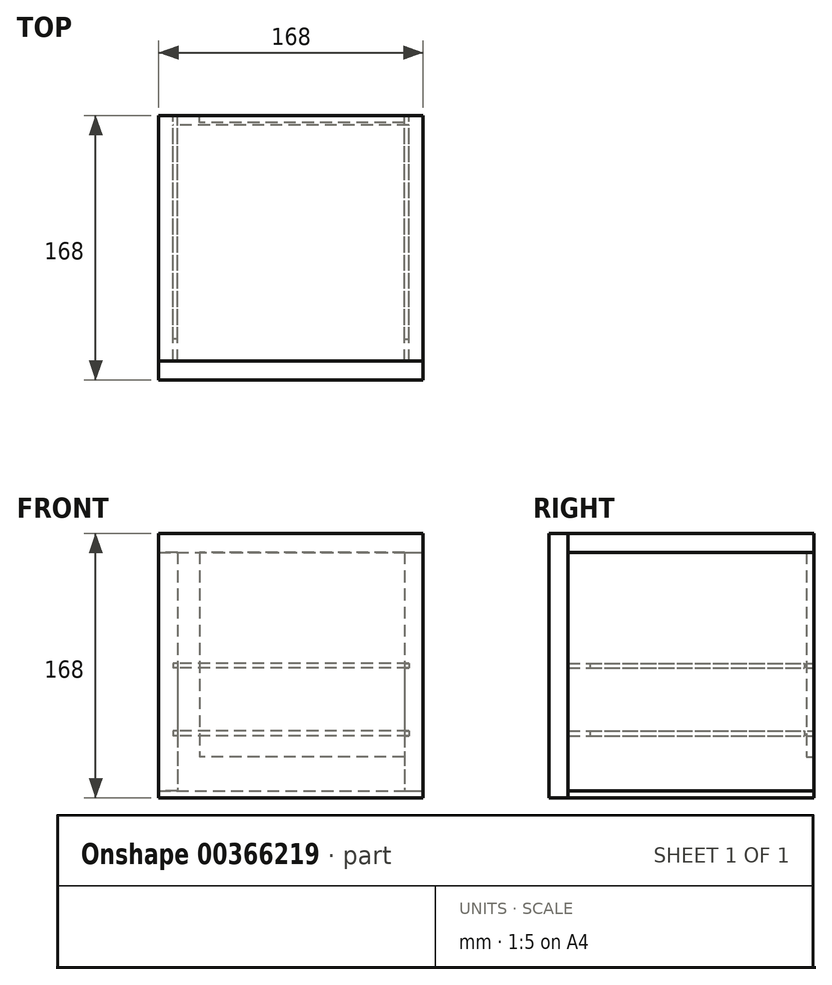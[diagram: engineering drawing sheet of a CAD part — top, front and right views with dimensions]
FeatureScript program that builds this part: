
annotation { "Feature Type Name" : "Feature", "Feature Type Description" : "" }
export const myFeature = defineFeature(function(context is Context, id is Id, definition is map)
    precondition{}
    {
        {
            var Q0;
            Q0=qCreatedBy(makeId("Front.planeOp"),FACE);
            var sketch = newSketch(context, id + "F0", { "sketchPlane" : qUnion([Q0])});
            skLineSegment(sketch, "E0.bottom", {"start": v(-84, 84.5) * mm, "end": v(84, 84.5) * mm});
            skLineSegment(sketch, "E0.top", {"start": v(-84, -83.5) * mm, "end": v(84, -83.5) * mm});
            skLineSegment(sketch, "E0.left", {"start": v(-84, 84.5) * mm, "end": v(-84, -83.5) * mm});
            skLineSegment(sketch, "E0.right", {"start": v(84, 84.5) * mm, "end": v(84, -83.5) * mm});
            skSolve(sketch);
        }
        {
            var Q0;
            Q0=qSketchRegion(id+"F0",true);
            var Q1;
            Q1=makeQuery(id+"F0.imprint","IMPRINT",FACE,{"disambiguationData":[TD([[makeQuery(id+"F0.imprint","IMPRINT",EDGE,{"derivedFrom":sQuery(id+"F0.wireOp",EDGE,"E0.bottom")}),-1.0]])]});
            extrude(context, id + "F1", {"entities" : qUnion([Q0, Q1]), "depth" : 12 * mm});
        }
        {
            var Q0;
            Q0=makeQuery(id+"F1.opExtrude","SWEPT_FACE",FACE,{"disambiguationData":[OSD([sQuery(id+"F0.wireOp",EDGE,"E0.right")])]});
            var sketch = newSketch(context, id + "F2", { "sketchPlane" : qUnion([Q0])});
            skLineSegment(sketch, "E1.bottom", {"start": v(0, 72.5) * mm, "end": v(156, 72.5) * mm});
            skLineSegment(sketch, "E1.top", {"start": v(0, -79) * mm, "end": v(156, -79) * mm});
            skLineSegment(sketch, "E1.left", {"start": v(0, 72.5) * mm, "end": v(0, -79) * mm});
            skLineSegment(sketch, "E1.right", {"start": v(156, 72.5) * mm, "end": v(156, -79) * mm});
            skSolve(sketch);
        }
        {
            var Q0;
            Q0=makeQuery(id+"F2.imprint","IMPRINT",FACE,{"disambiguationData":[TD([[makeQuery(id+"F2.imprint","IMPRINT",EDGE,{"derivedFrom":sQuery(id+"F2.wireOp",EDGE,"E1.bottom")}),-1.0]])]});
            extrude(context, id + "F3", {"entities" : qUnion([Q0]), "oppositeDirection" : true, "depth" : 12 * mm});
        }
        {
            var Q0;
            Q0=makeQuery(id+"F1.opExtrude","SWEPT_BODY",BODY,{"disambiguationData":[OSD([sQuery(id+"F0.wireOp",EDGE,"E0.bottom"),sQuery(id+"F0.wireOp",EDGE,"E0.top"),sQuery(id+"F0.wireOp",EDGE,"E0.left"),sQuery(id+"F0.wireOp",EDGE,"E0.right")])]});
            var Q1;
            Q1=qCreatedBy(makeId("Right.planeOp"),FACE);
            mirror(context, id + "F4", {"entities" : qUnion([Q0]), "mirrorPlane" : qUnion([Q1])});
        }
        {
            var Q0;
            Q0=makeQuery(id+"F1.opExtrude","SWEPT_FACE",FACE,{"disambiguationData":[OSD([sQuery(id+"F0.wireOp",EDGE,"E0.bottom")])]});
            var sketch = newSketch(context, id + "F5", { "sketchPlane" : qUnion([Q0])});
            skLineSegment(sketch, "E2.bottom", {"start": v(84, 0) * mm, "end": v(-84, 0) * mm});
            skLineSegment(sketch, "E2.top", {"start": v(84, 156) * mm, "end": v(-84, 156) * mm});
            skLineSegment(sketch, "E2.left", {"start": v(84, 0) * mm, "end": v(84, 156) * mm});
            skLineSegment(sketch, "E2.right", {"start": v(-84, 0) * mm, "end": v(-84, 156) * mm});
            skSolve(sketch);
        }
        {
            var Q0;
            Q0=makeQuery(id+"F5.imprint","IMPRINT",FACE,{"disambiguationData":[TD([[makeQuery(id+"F5.imprint","IMPRINT",EDGE,{"derivedFrom":sQuery(id+"F5.wireOp",EDGE,"E2.bottom")}),1.0]])]});
            extrude(context, id + "F6", {"entities" : qUnion([Q0]), "oppositeDirection" : true, "depth" : 12 * mm});
        }
        {
            var Q0;
            Q0=makeQuery(id+"F1.opExtrude","SWEPT_FACE",FACE,{"disambiguationData":[OSD([sQuery(id+"F0.wireOp",EDGE,"E0.top")])]});
            var sketch = newSketch(context, id + "F7", { "sketchPlane" : qUnion([Q0])});
            skLineSegment(sketch, "E3.bottom", {"start": v(-84, 0) * mm, "end": v(84, 0) * mm});
            skLineSegment(sketch, "E3.top", {"start": v(-84, -156) * mm, "end": v(84, -156) * mm});
            skLineSegment(sketch, "E3.left", {"start": v(-84, 0) * mm, "end": v(-84, -156) * mm});
            skLineSegment(sketch, "E3.right", {"start": v(84, 0) * mm, "end": v(84, -156) * mm});
            skSolve(sketch);
        }
        {
            var Q0;
            Q0=makeQuery(id+"F7.imprint","IMPRINT",FACE,{"disambiguationData":[TD([[makeQuery(id+"F7.imprint","IMPRINT",EDGE,{"derivedFrom":sQuery(id+"F7.wireOp",EDGE,"E3.bottom")}),-1.0]])]});
            extrude(context, id + "F8", {"entities" : qUnion([Q0]), "oppositeDirection" : true, "depth" : 4.5 * mm});
        }
        {
            var Q0;
            Q0=makeQuery(id+"F6.opExtrude","SWEPT_FACE",FACE,{"disambiguationData":[OSD([sQuery(id+"F5.wireOp",EDGE,"E2.top")])]});
            var sketch = newSketch(context, id + "F9", { "sketchPlane" : qUnion([Q0])});
            skLineSegment(sketch, "E4.bottom", {"start": v(-72, 72.5) * mm, "end": v(58, 72.5) * mm});
            skLineSegment(sketch, "E4.top", {"start": v(-72, -57.5) * mm, "end": v(58, -57.5) * mm});
            skLineSegment(sketch, "E4.left", {"start": v(-72, 72.5) * mm, "end": v(-72, -57.5) * mm});
            skLineSegment(sketch, "E4.right", {"start": v(58, 72.5) * mm, "end": v(58, -57.5) * mm});
            skSolve(sketch);
        }
        {
            var Q0;
            Q0=makeQuery(id+"F9.imprint","IMPRINT",FACE,{"disambiguationData":[TD([[makeQuery(id+"F9.imprint","IMPRINT",EDGE,{"derivedFrom":sQuery(id+"F9.wireOp",EDGE,"E4.bottom")}),-1.0]])]});
            extrude(context, id + "F10", {"entities" : qUnion([Q0]), "oppositeDirection" : true, "depth" : 4.5 * mm});
        }
        {
            var Q0;
            Q0=makeQuery(id+"F3.opExtrude","SWEPT_FACE",FACE,{"disambiguationData":[OSD([sQuery(id+"F2.wireOp",EDGE,"E1.right")])]});
            var sketch = newSketch(context, id + "F11", { "sketchPlane" : qUnion([Q0])});
            skLineSegment(sketch, "E5.bottom", {"start": v(-72, 2) * mm, "end": v(-75, 2) * mm});
            skLineSegment(sketch, "E5.top", {"start": v(-72, -1) * mm, "end": v(-75, -1) * mm});
            skLineSegment(sketch, "E5.left", {"start": v(-72, 2) * mm, "end": v(-72, -1) * mm});
            skLineSegment(sketch, "E5.right", {"start": v(-75, 2) * mm, "end": v(-75, -1) * mm});
            skLineSegment(sketch, "E6.bottom", {"start": v(-72, -41) * mm, "end": v(-75, -41) * mm});
            skLineSegment(sketch, "E6.top", {"start": v(-72, -44) * mm, "end": v(-75, -44) * mm});
            skLineSegment(sketch, "E6.left", {"start": v(-72, -41) * mm, "end": v(-72, -44) * mm});
            skLineSegment(sketch, "E6.right", {"start": v(-75, -41) * mm, "end": v(-75, -44) * mm});
            skSolve(sketch);
        }
        {
            var Q0;
            Q0=makeQuery(id+"F11.imprint","IMPRINT",FACE,{"disambiguationData":[TD([[makeQuery(id+"F11.imprint","IMPRINT",EDGE,{"derivedFrom":sQuery(id+"F11.wireOp",EDGE,"NvQbIwnB-lqE2-p2Xs-orIO-Tnx0DaEzGyps.bottom")}),1.0]])]});
            var Q1;
            Q1=makeQuery(id+"F11.imprint","IMPRINT",FACE,{"disambiguationData":[TD([[makeQuery(id+"F11.imprint","IMPRINT",EDGE,{"derivedFrom":sQuery(id+"F11.wireOp",EDGE,"E5.bottom")}),1.0]])]});
            var Q2;
            Q2=makeQuery(id+"F11.imprint","IMPRINT",FACE,{"disambiguationData":[TD([[makeQuery(id+"F11.imprint","IMPRINT",EDGE,{"derivedFrom":sQuery(id+"F11.wireOp",EDGE,"E6.bottom")}),1.0]])]});
            extrude(context, id + "F12", {"entities" : qUnion([Q0, Q1, Q2]), "operationType" : NewBodyOperationType.REMOVE, "oppositeDirection" : true, "depth" : 142 * mm});
        }
        {
            var Q0;
            Q0=makeQuery(id+"F3.opExtrude","SWEPT_BODY",BODY,{"disambiguationData":[OSD([sQuery(id+"F2.wireOp",EDGE,"E1.bottom"),sQuery(id+"F2.wireOp",EDGE,"E1.top"),sQuery(id+"F2.wireOp",EDGE,"E1.left"),sQuery(id+"F2.wireOp",EDGE,"E1.right")])]});
            var Q1;
            Q1=qCreatedBy(makeId("Right.planeOp"),FACE);
            mirror(context, id + "F13", {"entities" : qUnion([Q0]), "mirrorPlane" : qUnion([Q1])});
        }
        {
            var Q0;
            Q0=makeQuery(id+"F12.boolean.opBoolean","COPY",FACE,{"derivedFrom":makeQuery(id+"F12.opExtrude","SWEPT_FACE",FACE,{"disambiguationData":[OSD([sQuery(id+"F11.wireOp",EDGE,"E5.top")])]})});
            var sketch = newSketch(context, id + "F14", { "sketchPlane" : qUnion([Q0])});
            skLineSegment(sketch, "E7.bottom", {"start": v(75, 0) * mm, "end": v(-75, 0) * mm});
            skLineSegment(sketch, "E7.top", {"start": v(75, 150) * mm, "end": v(-75, 150) * mm});
            skLineSegment(sketch, "E7.left", {"start": v(75, 0) * mm, "end": v(75, 150) * mm});
            skLineSegment(sketch, "E7.right", {"start": v(-75, 0) * mm, "end": v(-75, 150) * mm});
            skSolve(sketch);
        }
        {
            var Q0;
            Q0=qSketchRegion(id+"F14",true);
            extrude(context, id + "F15", {"entities" : qUnion([Q0]), "depth" : 3 * mm});
        }
        {
            var Q0;
            Q0=makeQuery(id+"F15.opExtrude","SWEPT_BODY",BODY,{"disambiguationData":[OSD([sQuery(id+"F14.wireOp",EDGE,"E7.bottom"),sQuery(id+"F14.wireOp",EDGE,"E7.top"),sQuery(id+"F14.wireOp",EDGE,"E7.left"),sQuery(id+"F14.wireOp",EDGE,"E7.right")])]});
            transform(context, id + "F16", {"entities" : qUnion([Q0]), "transformType" : TransformType.TRANSLATION_3D, "dx" : 0 * mm, "dy" : 0 * mm, "dz" : -43 * mm, "makeCopy" : true});
        }
    });
